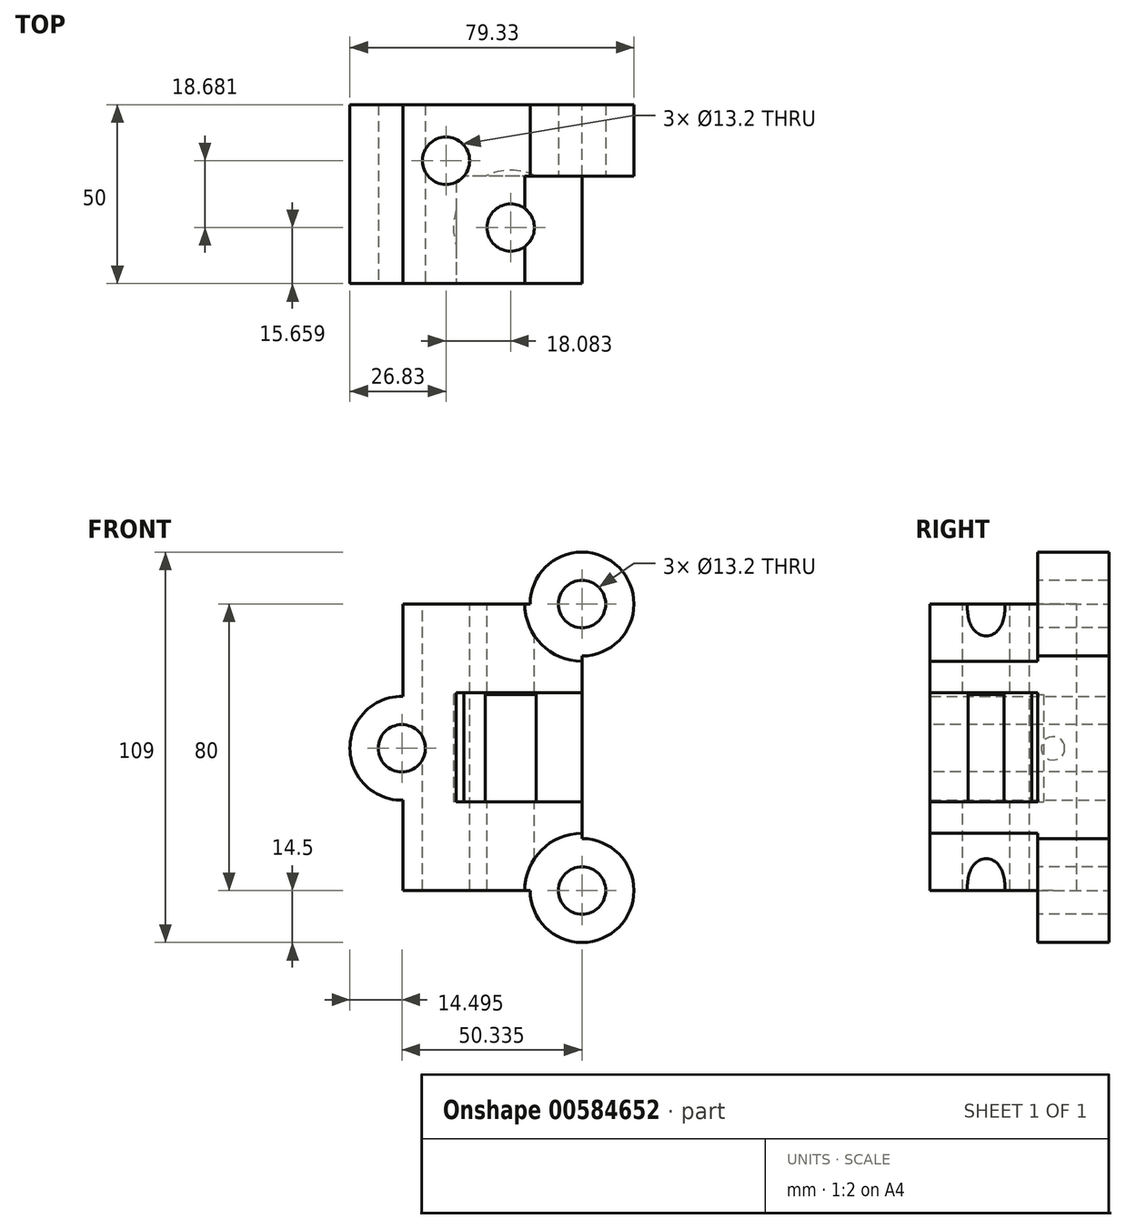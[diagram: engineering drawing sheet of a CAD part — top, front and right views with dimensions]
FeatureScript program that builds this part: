
annotation { "Feature Type Name" : "Feature", "Feature Type Description" : "" }
export const myFeature = defineFeature(function(context is Context, id is Id, definition is map)
    precondition{}
    {
        {
            var Q0;
            Q0=qCreatedBy(makeId("Front.planeOp"),FACE);
            var sketch = newSketch(context, id + "F0", { "sketchPlane" : qUnion([Q0])});
            skLineSegment(sketch, "E0.bottom", {"start": v(25, -40) * mm, "end": v(-25, -40) * mm});
            skLineSegment(sketch, "E0.top", {"start": v(25, 40) * mm, "end": v(-25, 40) * mm});
            skLineSegment(sketch, "E0.left", {"start": v(25, -40) * mm, "end": v(25, 40) * mm});
            skLineSegment(sketch, "E0.right", {"start": v(-25, -40) * mm, "end": v(-25, 40) * mm});
            skPoint(sketch, "E0.middle", {"position": v(0, 0) * mm});
            skCircle(sketch, "E1", {"center": v(25, 40) * mm, "radius": 14.5 * mm});
            skCircle(sketch, "E2", {"center": v(25, -40) * mm, "radius": 14.5 * mm});
            skCircle(sketch, "E3", {"center": v(-25.33, -0.28) * mm, "radius": 14.5 * mm});
            skSolve(sketch);
        }
        {
            var Q0;
            Q0 = qSketchRegion(id + "F0", true);
            extrude(context, id + "F1", {"entities" : qUnion([Q0]), "endBound" : BoundingType.SYMMETRIC, "depth" : 50 * mm, "offsetDistance" : 25 * mm});
        }
        {
            var Q0;
            Q0=makeQuery(id+"F1.opExtrude","CAP_FACE",FACE,{"disambiguationData":[OSD([sQuery(id+"F0.wireOp",EDGE,"E0.bottom"),sQuery(id+"F0.wireOp",EDGE,"E0.top"),sQuery(id+"F0.wireOp",EDGE,"E0.left"),sQuery(id+"F0.wireOp",EDGE,"E0.right"),sQuery(id+"F0.wireOp",EDGE,"E1"),sQuery(id+"F0.wireOp",EDGE,"E2"),sQuery(id+"F0.wireOp",EDGE,"E3")])],"isStart":false});
            var sketch = newSketch(context, id + "F2", { "sketchPlane" : qUnion([Q0])});
            skPoint(sketch, "E4", {"position": v(25, 40) * mm});
            skPoint(sketch, "E5", {"position": v(25, -40) * mm});
            skPoint(sketch, "E6", {"position": v(-25.33, -0.28) * mm});
            skSolve(sketch);
        }
        {
            var Q0;
            Q0=sQuery(id+"F2.wireOp",VERTEX,"E4");
            var Q1;
            Q1=sQuery(id+"F2.wireOp",VERTEX,"E6");
            var Q2;
            Q2=sQuery(id+"F2.wireOp",VERTEX,"E5");
            var Q3;
            Q3=makeQuery(id+"F1.opExtrude","SWEPT_BODY",BODY,{"disambiguationData":[OSD([sQuery(id+"F0.wireOp",EDGE,"E0.bottom"),sQuery(id+"F0.wireOp",EDGE,"E0.top"),sQuery(id+"F0.wireOp",EDGE,"E0.left"),sQuery(id+"F0.wireOp",EDGE,"E0.right"),sQuery(id+"F0.wireOp",EDGE,"E1"),sQuery(id+"F0.wireOp",EDGE,"E2"),sQuery(id+"F0.wireOp",EDGE,"E3")])]});
            hole(context, id + "F3", {"style" : HoleStyle.C_BORE, "endStyle" : HoleEndStyle.THROUGH, "holeDiameter" : 13.2 * mm, "cBoreDiameter" : 19.25 * mm, "cBoreDepth" : 0 * mm, "majorDiameter" : 5 * mm, "isTappedThrough" : true, "tappedDepth" : 12 * mm, "tapClearance" : 3, "startFromSketch" : true, "locations" : qUnion([Q0, Q1, Q2]), "scope" : qUnion([Q3])});
        }
        {
            var Q0;
            Q0=makeQuery(id+"F1.opExtrude","SWEPT_FACE",FACE,{"disambiguationData":[OSD([sQuery(id+"F0.wireOp",EDGE,"E0.top")])]});
            var sketch = newSketch(context, id + "F4", { "sketchPlane" : qUnion([Q0])});
            skLineSegment(sketch, "E7.bottom", {"start": v(5.08, 9.34) * mm, "end": v(-13, 9.34) * mm});
            skLineSegment(sketch, "E7.top", {"start": v(5.08, -9.34) * mm, "end": v(-13, -9.34) * mm});
            skLineSegment(sketch, "E7.left", {"start": v(-13, -9.34) * mm, "end": v(-13, 9.34) * mm});
            skLineSegment(sketch, "E7.right", {"start": v(5.08, -9.34) * mm, "end": v(5.08, 9.34) * mm});
            skPoint(sketch, "E8", {"position": v(-13, 9.34) * mm});
            skPoint(sketch, "E9", {"position": v(5.08, -9.34) * mm});
            skSolve(sketch);
        }
        {
            var Q0;
            Q0=sQuery(id+"F4.wireOp",VERTEX,"E8");
            var Q1;
            Q1=sQuery(id+"F4.wireOp",VERTEX,"E9");
            var Q2;
            Q2=makeQuery(id+"F1.opExtrude","SWEPT_BODY",BODY,{"disambiguationData":[OSD([sQuery(id+"F0.wireOp",EDGE,"E0.bottom"),sQuery(id+"F0.wireOp",EDGE,"E0.top"),sQuery(id+"F0.wireOp",EDGE,"E0.left"),sQuery(id+"F0.wireOp",EDGE,"E0.right"),sQuery(id+"F0.wireOp",EDGE,"E1"),sQuery(id+"F0.wireOp",EDGE,"E2"),sQuery(id+"F0.wireOp",EDGE,"E3")])]});
            hole(context, id + "F5", {"style" : HoleStyle.C_BORE, "endStyle" : HoleEndStyle.THROUGH, "holeDiameter" : 13.2 * mm, "cBoreDiameter" : 19.25 * mm, "cBoreDepth" : 0 * mm, "majorDiameter" : 5 * mm, "isTappedThrough" : true, "tappedDepth" : 12 * mm, "tapClearance" : 3, "startFromSketch" : true, "locations" : qUnion([Q0, Q1]), "scope" : qUnion([Q2])});
        }
        {
            var Q0;
            Q0=makeQuery(id+"F1.opExtrude","CAP_FACE",FACE,{"disambiguationData":[OSD([sQuery(id+"F0.wireOp",EDGE,"E0.bottom"),sQuery(id+"F0.wireOp",EDGE,"E0.top"),sQuery(id+"F0.wireOp",EDGE,"E0.left"),sQuery(id+"F0.wireOp",EDGE,"E0.right"),sQuery(id+"F0.wireOp",EDGE,"E1"),sQuery(id+"F0.wireOp",EDGE,"E2"),sQuery(id+"F0.wireOp",EDGE,"E3")])],"isStart":false});
            var sketch = newSketch(context, id + "F6", { "sketchPlane" : qUnion([Q0])});
            skLineSegment(sketch, "E10.bottom", {"start": v(29.9, -15.25) * mm, "end": v(-10.1, -15.25) * mm});
            skLineSegment(sketch, "E10.top", {"start": v(29.9, 15.25) * mm, "end": v(-10.1, 15.25) * mm});
            skLineSegment(sketch, "E10.left", {"start": v(29.9, -15.25) * mm, "end": v(29.9, 15.25) * mm});
            skLineSegment(sketch, "E10.right", {"start": v(-10.1, -15.25) * mm, "end": v(-10.1, 15.25) * mm});
            skPoint(sketch, "E10.middle", {"position": v(9.9, 0) * mm});
            skSolve(sketch);
        }
        {
            var Q0;
            Q0 = qSketchRegion(id + "F6", true);
            extrude(context, id + "F7", {"entities" : qUnion([Q0]), "operationType" : NewBodyOperationType.REMOVE, "oppositeDirection" : true, "depth" : 30 * mm, "offsetDistance" : 25 * mm});
        }
        {
            var Q0;
            Q0=makeQuery(id+"F7.boolean.opBoolean","COPY",FACE,{"derivedFrom":makeQuery(id+"F7.opExtrude","SWEPT_FACE",FACE,{"disambiguationData":[OSD([sQuery(id+"F6.wireOp",EDGE,"E10.bottom")])]})});
            var sketch = newSketch(context, id + "F8", { "sketchPlane" : qUnion([Q0])});
            skCircle(sketch, "E11", {"center": v(5.08, -9.34) * mm, "radius": 16 * mm});
            skSolve(sketch);
        }
        {
            var Q0;
            Q0 = qSketchRegion(id + "F8", true);
            extrude(context, id + "F9", {"entities" : qUnion([Q0]), "operationType" : NewBodyOperationType.REMOVE, "oppositeDirection" : true, "depth" : -30 * mm, "offsetDistance" : 25 * mm});
        }
        {
            var Q0;
            Q0=makeQuery(id+"F1.opExtrude","CAP_FACE",FACE,{"disambiguationData":[OSD([sQuery(id+"F0.wireOp",EDGE,"E0.bottom"),sQuery(id+"F0.wireOp",EDGE,"E0.top"),sQuery(id+"F0.wireOp",EDGE,"E0.left"),sQuery(id+"F0.wireOp",EDGE,"E0.right"),sQuery(id+"F0.wireOp",EDGE,"E1"),sQuery(id+"F0.wireOp",EDGE,"E2"),sQuery(id+"F0.wireOp",EDGE,"E3")])],"isStart":false});
            var sketch = newSketch(context, id + "F10", { "sketchPlane" : qUnion([Q0])});
            skCircle(sketch, "E12", {"center": v(25, 40) * mm, "radius": 16 * mm});
            skCircle(sketch, "E13", {"center": v(25, -40) * mm, "radius": 16 * mm});
            skSolve(sketch);
        }
        {
            var Q0;
            Q0 = qSketchRegion(id + "F10", true);
            extrude(context, id + "F11", {"entities" : qUnion([Q0]), "operationType" : NewBodyOperationType.REMOVE, "oppositeDirection" : true, "depth" : 30 * mm, "offsetDistance" : 25 * mm});
        }
    });
